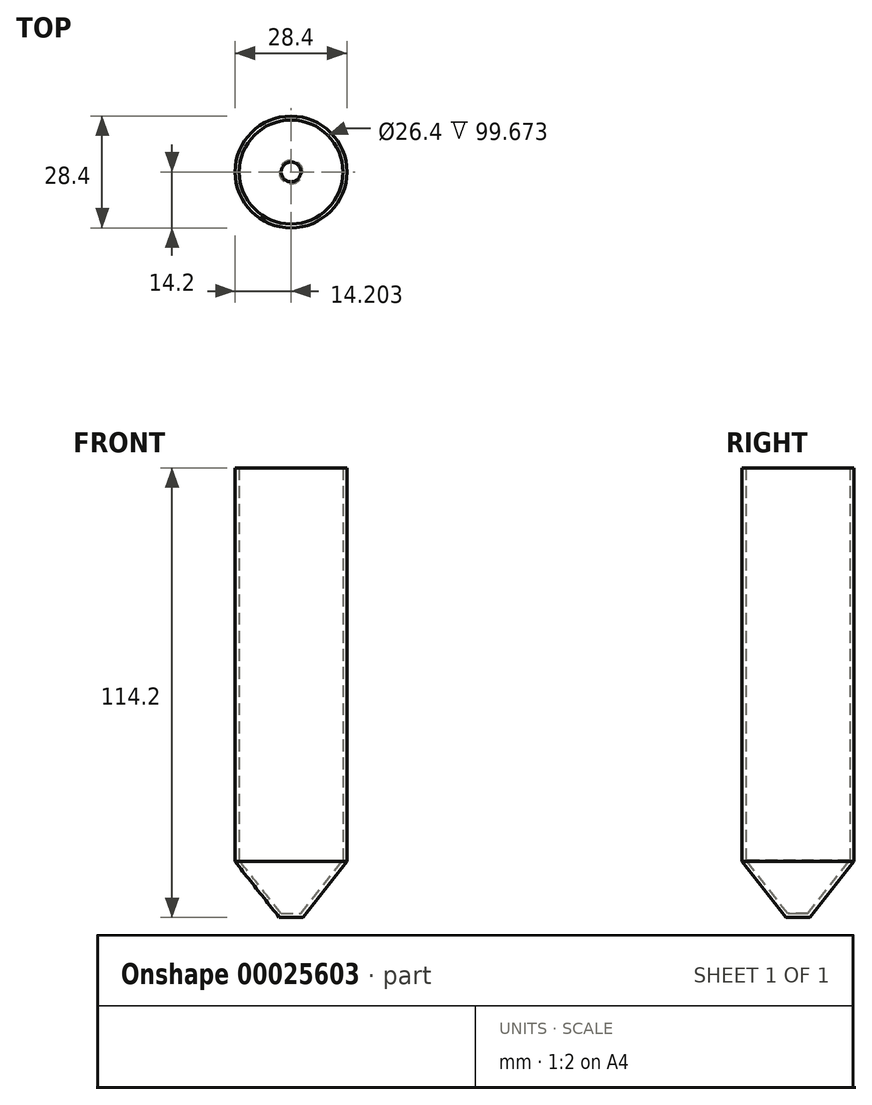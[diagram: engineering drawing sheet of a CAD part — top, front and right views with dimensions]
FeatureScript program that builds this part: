
annotation { "Feature Type Name" : "Feature", "Feature Type Description" : "" }
export const myFeature = defineFeature(function(context is Context, id is Id, definition is map)
    precondition{}
    {
        {
            var Q0;
            Q0=qCreatedBy(makeId("Front.planeOp"),FACE);
            var sketch = newSketch(context, id + "F0", { "sketchPlane" : qUnion([Q0])});
            skLineSegment(sketch, "E0", {"start": v(20.57, 60.39) * mm, "end": v(20.57, -39.63) * mm});
            skLineSegment(sketch, "E1", {"start": v(6.37, -53.81) * mm, "end": v(6.37, 60.39) * mm, "construction": true});
            skLineSegment(sketch, "E2", {"start": v(20.57, 60.39) * mm, "end": v(6.37, 60.39) * mm, "construction": true});
            skLineSegment(sketch, "E3", {"start": v(6.37, -53.81) * mm, "end": v(9.37, -53.81) * mm});
            skLineSegment(sketch, "E4", {"start": v(9.37, -53.81) * mm, "end": v(20.57, -39.63) * mm});
            skLineSegment(sketch, "E5.0", {"start": v(6.37, -52.81) * mm, "end": v(8.89, -52.81) * mm});
            skLineSegment(sketch, "E5.1", {"start": v(8.89, -52.81) * mm, "end": v(19.57, -39.29) * mm});
            skLineSegment(sketch, "E5.2", {"start": v(19.57, 60.39) * mm, "end": v(19.57, -39.29) * mm});
            skLineSegment(sketch, "E6", {"start": v(19.57, 60.39) * mm, "end": v(20.57, 60.39) * mm});
            skLineSegment(sketch, "E7", {"start": v(6.37, -53.81) * mm, "end": v(6.37, -52.81) * mm});
            skSolve(sketch);
        }
        {
            var Q0;
            Q0=makeQuery(id+"F0.imprint","IMPRINT",FACE,{"disambiguationData":[TD([[makeQuery(id+"F0.imprint","IMPRINT",EDGE,{"derivedFrom":sQuery(id+"F0.wireOp",EDGE,"E0")}),-1.0]])]});
            var Q1;
            Q1=sQuery(id+"F0.wireOp",EDGE,"E1");
            revolve(context, id + "F1", {"entities" : qUnion([Q0]), "axis" : qUnion([Q1]), "revolveType" : RevolveType.FULL});
        }
    });
